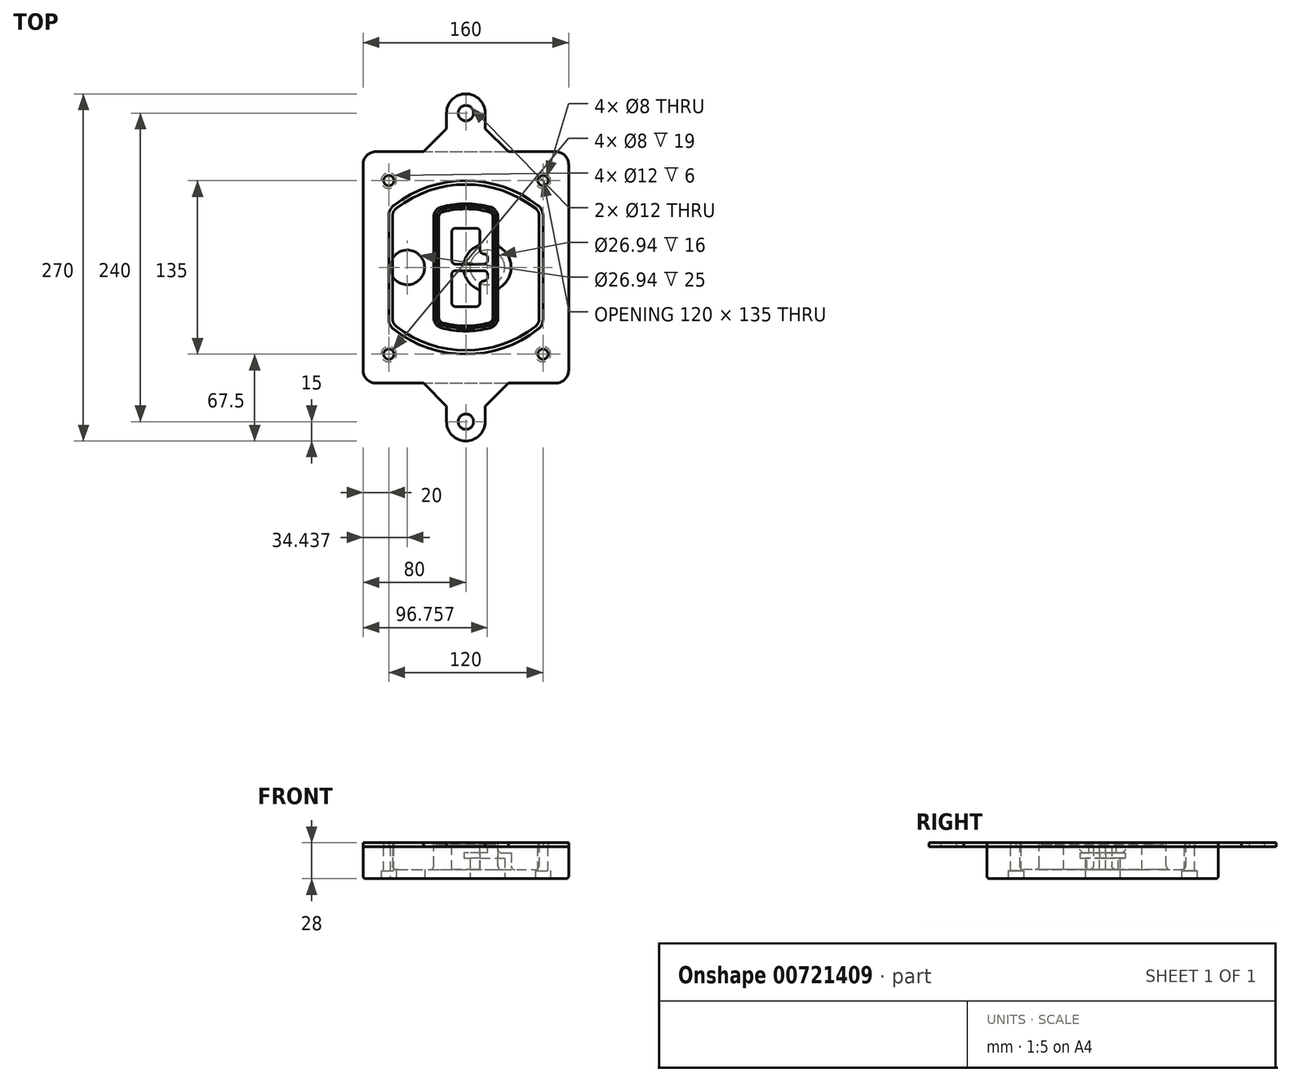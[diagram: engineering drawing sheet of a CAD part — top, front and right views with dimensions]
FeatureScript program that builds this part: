
annotation { "Feature Type Name" : "Feature", "Feature Type Description" : "" }
export const myFeature = defineFeature(function(context is Context, id is Id, definition is map)
    precondition{}
    {
        {
            var Q0;
            Q0=qCreatedBy(makeId("Top.planeOp"),FACE);
            var sketch = newSketch(context, id + "F0", { "sketchPlane" : qUnion([Q0])});
            skPoint(sketch, "E0.rect.middle", {"position": v(0, 0) * mm});
            skLineSegment(sketch, "E1.bottom", {"start": v(-70, -90) * mm, "end": v(70, -90) * mm});
            skLineSegment(sketch, "E1.top", {"start": v(-70, 90) * mm, "end": v(70, 90) * mm});
            skLineSegment(sketch, "E1.left", {"start": v(-80, -80) * mm, "end": v(-80, 80) * mm});
            skLineSegment(sketch, "E1.right", {"start": v(80, -80) * mm, "end": v(80, 80) * mm});
            skLineSegment(sketch, "E2", {"start": v(-80, 90) * mm, "end": v(80, -90) * mm, "construction": true});
            skLineSegment(sketch, "E3", {"start": v(80, 90) * mm, "end": v(-80, -90) * mm, "construction": true});
            skCircle(sketch, "E4", {"center": v(-60, 67.5) * mm, "radius": 4 * mm});
            skCircle(sketch, "E5", {"center": v(60, 67.5) * mm, "radius": 4 * mm});
            skCircle(sketch, "E6", {"center": v(60, -67.5) * mm, "radius": 4 * mm});
            skCircle(sketch, "E7", {"center": v(-60, -67.5) * mm, "radius": 4 * mm});
            skLineSegment(sketch, "E8", {"start": v(-60, 67.5) * mm, "end": v(60, 67.5) * mm, "construction": true});
            skLineSegment(sketch, "E9", {"start": v(60, 67.5) * mm, "end": v(60, -67.5) * mm, "construction": true});
            skLineSegment(sketch, "E10", {"start": v(60, -67.5) * mm, "end": v(-60, -67.5) * mm, "construction": true});
            skLineSegment(sketch, "E11", {"start": v(-60, -67.5) * mm, "end": v(-60, 67.5) * mm, "construction": true});
            skLineSegment(sketch, "E12", {"start": v(-60, 40.3) * mm, "end": v(-60, -40.3) * mm});
            skLineSegment(sketch, "E13", {"start": v(60, 40.3) * mm, "end": v(60, -40.3) * mm});
            skArc(sketch, "E14", {"start": v(56.15, 48.18) * mm, "mid": v(0, 67.5) * mm, "end": v(-56.15, 48.18) * mm});
            skArc(sketch, "E15", {"start": v(-56.15, -48.18) * mm, "mid": v(0, -67.5) * mm, "end": v(56.15, -48.18) * mm});
            skLineSegment(sketch, "E16", {"start": v(-60, 0) * mm, "end": v(60, 0) * mm, "construction": true});
            skPoint(sketch, "E17.visualSharp", {"position": v(-60, -45) * mm});
            skArc(sketch, "E17.filletArc", {"start": v(-60, -40.3) * mm, "mid": v(-58.99, -44.68) * mm, "end": v(-56.15, -48.18) * mm});
            skPoint(sketch, "E18.visualSharp", {"position": v(-60, 45) * mm});
            skArc(sketch, "E18.filletArc", {"start": v(-56.15, 48.18) * mm, "mid": v(-58.99, 44.68) * mm, "end": v(-60, 40.3) * mm});
            skPoint(sketch, "E19.visualSharp", {"position": v(60, 45) * mm});
            skArc(sketch, "E19.filletArc", {"start": v(60, 40.3) * mm, "mid": v(58.99, 44.68) * mm, "end": v(56.15, 48.18) * mm});
            skPoint(sketch, "E20.visualSharp", {"position": v(60, -45) * mm});
            skArc(sketch, "E20.filletArc", {"start": v(56.15, -48.18) * mm, "mid": v(58.99, -44.68) * mm, "end": v(60, -40.3) * mm});
            skPoint(sketch, "E21.visualSharp", {"position": v(-80, 90) * mm});
            skArc(sketch, "E21.filletArc", {"start": v(-70, 90) * mm, "mid": v(-77.07, 87.07) * mm, "end": v(-80, 80) * mm});
            skPoint(sketch, "E22.visualSharp", {"position": v(80, 90) * mm});
            skArc(sketch, "E22.filletArc", {"start": v(80, 80) * mm, "mid": v(77.07, 87.07) * mm, "end": v(70, 90) * mm});
            skPoint(sketch, "E23.visualSharp", {"position": v(80, -90) * mm});
            skArc(sketch, "E23.filletArc", {"start": v(70, -90) * mm, "mid": v(77.07, -87.07) * mm, "end": v(80, -80) * mm});
            skPoint(sketch, "E24.visualSharp", {"position": v(-80, -90) * mm});
            skArc(sketch, "E24.filletArc", {"start": v(-80, -80) * mm, "mid": v(-77.07, -87.07) * mm, "end": v(-70, -90) * mm});
            skArc(sketch, "E25.0", {"start": v(57, 40.3) * mm, "mid": v(56.3, 43.36) * mm, "end": v(54.3, 45.81) * mm});
            skLineSegment(sketch, "E25.1", {"start": v(57, 40.3) * mm, "end": v(57, -40.3) * mm});
            skArc(sketch, "E25.2", {"start": v(54.3, -45.81) * mm, "mid": v(56.3, -43.36) * mm, "end": v(57, -40.3) * mm});
            skArc(sketch, "E25.3", {"start": v(-54.3, -45.81) * mm, "mid": v(0, -64.5) * mm, "end": v(54.3, -45.81) * mm});
            skArc(sketch, "E25.4", {"start": v(-57, -40.3) * mm, "mid": v(-56.3, -43.36) * mm, "end": v(-54.3, -45.81) * mm});
            skArc(sketch, "E25.5", {"start": v(54.3, 45.81) * mm, "mid": v(0, 64.5) * mm, "end": v(-54.3, 45.81) * mm});
            skLineSegment(sketch, "E25.6", {"start": v(-57, 40.3) * mm, "end": v(-57, -40.3) * mm});
            skArc(sketch, "E25.7", {"start": v(-54.3, 45.81) * mm, "mid": v(-56.3, 43.36) * mm, "end": v(-57, 40.3) * mm});
            skArc(sketch, "E26.0", {"start": v(-58.62, 51.33) * mm, "mid": v(-62.58, 46.43) * mm, "end": v(-64, 40.3) * mm});
            skArc(sketch, "E26.1", {"start": v(58.62, 51.33) * mm, "mid": v(0, 71.5) * mm, "end": v(-58.62, 51.33) * mm});
            skArc(sketch, "E26.2", {"start": v(64, 40.3) * mm, "mid": v(62.58, 46.43) * mm, "end": v(58.62, 51.33) * mm});
            skLineSegment(sketch, "E26.3", {"start": v(64, 40.3) * mm, "end": v(64, -40.3) * mm});
            skArc(sketch, "E26.4", {"start": v(58.62, -51.33) * mm, "mid": v(62.58, -46.43) * mm, "end": v(64, -40.3) * mm});
            skLineSegment(sketch, "E26.5", {"start": v(-64, 40.3) * mm, "end": v(-64, -40.3) * mm});
            skArc(sketch, "E26.6", {"start": v(-58.62, -51.33) * mm, "mid": v(0, -71.5) * mm, "end": v(58.62, -51.33) * mm});
            skArc(sketch, "E26.7", {"start": v(-64, -40.3) * mm, "mid": v(-62.58, -46.43) * mm, "end": v(-58.62, -51.33) * mm});
            skSolve(sketch);
        }
        {
            var Q0;
            Q0=makeQuery(id+"F0.imprint","IMPRINT",FACE,{"disambiguationData":[TD([[makeQuery(id+"F0.imprint","IMPRINT",EDGE,{"derivedFrom":sQuery(id+"F0.wireOp",EDGE,"E1.bottom")}),1.0]])]});
            var Q1;
            Q1=makeQuery(id+"F0.imprint","IMPRINT",FACE,{"disambiguationData":[TD([[makeQuery(id+"F0.imprint","IMPRINT",EDGE,{"derivedFrom":sQuery(id+"F0.wireOp",EDGE,"E12")}),1.0]])]});
            var Q2;
            Q2=makeQuery(id+"F0.imprint","IMPRINT",FACE,{"disambiguationData":[TD([[makeQuery(id+"F0.imprint","IMPRINT",EDGE,{"derivedFrom":sQuery(id+"F0.wireOp",EDGE,"E25.0")}),1.0]])]});
            var Q3;
            Q3=makeQuery(id+"F0.imprint","IMPRINT",FACE,{"disambiguationData":[TD([[makeQuery(id+"F0.imprint","IMPRINT",EDGE,{"derivedFrom":sQuery(id+"F0.wireOp",EDGE,"E12")}),-1.0]])]});
            extrude(context, id + "F1", {"entities" : qUnion([Q0, Q1, Q2, Q3]), "oppositeDirection" : true, "depth" : 25 * mm});
        }
        {
            var Q0;
            Q0=makeQuery(id+"F0.imprint","IMPRINT",FACE,{"disambiguationData":[TD([[makeQuery(id+"F0.imprint","IMPRINT",EDGE,{"derivedFrom":sQuery(id+"F0.wireOp",EDGE,"E12")}),1.0]])]});
            extrude(context, id + "F2", {"entities" : qUnion([Q0]), "operationType" : NewBodyOperationType.ADD, "depth" : 3 * mm, "offsetDistance" : 25 * mm});
        }
        {
            var Q0;
            Q0=makeQuery(id+"F0.imprint","IMPRINT",FACE,{"disambiguationData":[TD([[makeQuery(id+"F0.imprint","IMPRINT",EDGE,{"derivedFrom":sQuery(id+"F0.wireOp",EDGE,"E25.0")}),1.0]])]});
            extrude(context, id + "F3", {"entities" : qUnion([Q0]), "operationType" : NewBodyOperationType.REMOVE, "oppositeDirection" : true, "depth" : 18 * mm});
        }
        {
            var Q0;
            Q0=makeQuery(id+"F2.opExtrude","CAP_FACE",FACE,{"disambiguationData":[OSD([sQuery(id+"F0.wireOp",EDGE,"E12"),sQuery(id+"F0.wireOp",EDGE,"E13"),sQuery(id+"F0.wireOp",EDGE,"E14"),sQuery(id+"F0.wireOp",EDGE,"E15"),sQuery(id+"F0.wireOp",EDGE,"E17.filletArc"),sQuery(id+"F0.wireOp",EDGE,"E18.filletArc"),sQuery(id+"F0.wireOp",EDGE,"E19.filletArc"),sQuery(id+"F0.wireOp",EDGE,"E20.filletArc"),sQuery(id+"F0.wireOp",EDGE,"E25.0"),sQuery(id+"F0.wireOp",EDGE,"E25.1"),sQuery(id+"F0.wireOp",EDGE,"E25.2"),sQuery(id+"F0.wireOp",EDGE,"E25.3"),sQuery(id+"F0.wireOp",EDGE,"E25.4"),sQuery(id+"F0.wireOp",EDGE,"E25.5"),sQuery(id+"F0.wireOp",EDGE,"E25.6"),sQuery(id+"F0.wireOp",EDGE,"E25.7")])],"isStart":false});
            var sketch = newSketch(context, id + "F4", { "sketchPlane" : qUnion([Q0])});
            skArc(sketch, "E27.0", {"start": v(-19.08, -46.97) * mm, "mid": v(0, -49.5) * mm, "end": v(19.08, -46.97) * mm});
            skArc(sketch, "E28.0", {"start": v(19.08, 46.97) * mm, "mid": v(0, 49.5) * mm, "end": v(-19.08, 46.97) * mm});
            skLineSegment(sketch, "E29", {"start": v(-25, 39.25) * mm, "end": v(-25, -39.25) * mm});
            skLineSegment(sketch, "E30", {"start": v(25, 39.25) * mm, "end": v(25, -39.25) * mm});
            skLineSegment(sketch, "E31", {"start": v(-25, 45.1) * mm, "end": v(25, 45.1) * mm, "construction": true});
            skLineSegment(sketch, "E32", {"start": v(-25, -45.1) * mm, "end": v(25, -45.1) * mm, "construction": true});
            skPoint(sketch, "E33.visualSharp", {"position": v(-25, 45.1) * mm});
            skArc(sketch, "E33.filletArc", {"start": v(-19.08, 46.97) * mm, "mid": v(-23.35, 44.11) * mm, "end": v(-25, 39.25) * mm});
            skPoint(sketch, "E34.visualSharp", {"position": v(25, 45.1) * mm});
            skArc(sketch, "E34.filletArc", {"start": v(25, 39.25) * mm, "mid": v(23.35, 44.11) * mm, "end": v(19.08, 46.97) * mm});
            skPoint(sketch, "E35.visualSharp", {"position": v(25, -45.1) * mm});
            skArc(sketch, "E35.filletArc", {"start": v(19.08, -46.97) * mm, "mid": v(23.35, -44.11) * mm, "end": v(25, -39.25) * mm});
            skPoint(sketch, "E36.visualSharp", {"position": v(-25, -45.1) * mm});
            skArc(sketch, "E36.filletArc", {"start": v(-25, -39.25) * mm, "mid": v(-23.35, -44.11) * mm, "end": v(-19.08, -46.97) * mm});
            skArc(sketch, "E37.0", {"start": v(54.3, 45.81) * mm, "mid": v(0, 64.5) * mm, "end": v(-54.3, 45.81) * mm});
            skArc(sketch, "E37.1", {"start": v(-54.3, 45.81) * mm, "mid": v(-56.3, 43.36) * mm, "end": v(-57, 40.3) * mm});
            skLineSegment(sketch, "E37.2", {"start": v(-57, 40.3) * mm, "end": v(-57, -40.3) * mm});
            skArc(sketch, "E37.3", {"start": v(-57, -40.3) * mm, "mid": v(-56.3, -43.36) * mm, "end": v(-54.3, -45.81) * mm});
            skArc(sketch, "E37.4", {"start": v(-54.3, -45.81) * mm, "mid": v(0, -64.5) * mm, "end": v(54.3, -45.81) * mm});
            skArc(sketch, "E37.5", {"start": v(54.3, -45.81) * mm, "mid": v(56.3, -43.36) * mm, "end": v(57, -40.3) * mm});
            skLineSegment(sketch, "E37.6", {"start": v(57, 40.3) * mm, "end": v(57, -40.3) * mm});
            skArc(sketch, "E37.7", {"start": v(57, 40.3) * mm, "mid": v(56.3, 43.36) * mm, "end": v(54.3, 45.81) * mm});
            skLineSegment(sketch, "E38.0", {"start": v(23, 39.25) * mm, "end": v(23, -39.25) * mm});
            skArc(sketch, "E38.1", {"start": v(18.56, -45.04) * mm, "mid": v(21.76, -42.9) * mm, "end": v(23, -39.25) * mm});
            skArc(sketch, "E38.2", {"start": v(-18.56, -45.04) * mm, "mid": v(0, -47.5) * mm, "end": v(18.56, -45.04) * mm});
            skArc(sketch, "E38.3", {"start": v(-23, -39.25) * mm, "mid": v(-21.76, -42.9) * mm, "end": v(-18.56, -45.04) * mm});
            skLineSegment(sketch, "E38.4", {"start": v(-23, 39.25) * mm, "end": v(-23, -39.25) * mm});
            skArc(sketch, "E38.5", {"start": v(23, 39.25) * mm, "mid": v(21.76, 42.9) * mm, "end": v(18.56, 45.04) * mm});
            skArc(sketch, "E38.6", {"start": v(-18.56, 45.04) * mm, "mid": v(-21.76, 42.9) * mm, "end": v(-23, 39.25) * mm});
            skArc(sketch, "E38.7", {"start": v(18.56, 45.04) * mm, "mid": v(0, 47.5) * mm, "end": v(-18.56, 45.04) * mm});
            skArc(sketch, "E39.0", {"start": v(21, 39.25) * mm, "mid": v(20.18, 41.68) * mm, "end": v(18.04, 43.1) * mm});
            skLineSegment(sketch, "E39.1", {"start": v(21, 39.25) * mm, "end": v(21, -39.25) * mm});
            skArc(sketch, "E39.2", {"start": v(18.04, -43.1) * mm, "mid": v(20.18, -41.68) * mm, "end": v(21, -39.25) * mm});
            skArc(sketch, "E39.3", {"start": v(-18.04, -43.1) * mm, "mid": v(0, -45.5) * mm, "end": v(18.04, -43.1) * mm});
            skArc(sketch, "E39.4", {"start": v(-21, -39.25) * mm, "mid": v(-20.18, -41.68) * mm, "end": v(-18.04, -43.1) * mm});
            skArc(sketch, "E39.5", {"start": v(18.04, 43.1) * mm, "mid": v(0, 45.5) * mm, "end": v(-18.04, 43.1) * mm});
            skLineSegment(sketch, "E39.6", {"start": v(-21, 39.25) * mm, "end": v(-21, -39.25) * mm});
            skArc(sketch, "E39.7", {"start": v(-18.04, 43.1) * mm, "mid": v(-20.18, 41.68) * mm, "end": v(-21, 39.25) * mm});
            skLineSegment(sketch, "E40", {"start": v(-25, 0) * mm, "end": v(25, 0) * mm, "construction": true});
            skLineSegment(sketch, "E41", {"start": v(-11, 5.5) * mm, "end": v(-11, 27.5) * mm});
            skLineSegment(sketch, "E42", {"start": v(-8, 30.5) * mm, "end": v(8, 30.5) * mm});
            skLineSegment(sketch, "E43", {"start": v(11, 27.5) * mm, "end": v(11, 13.5) * mm});
            skLineSegment(sketch, "E44", {"start": v(14, 10.5) * mm, "end": v(14, 10.5) * mm});
            skLineSegment(sketch, "E45", {"start": v(17, 7.5) * mm, "end": v(17, 5.5) * mm});
            skLineSegment(sketch, "E46", {"start": v(14, 2.5) * mm, "end": v(-8, 2.5) * mm});
            skPoint(sketch, "E47.visualSharp", {"position": v(-11, 30.5) * mm});
            skArc(sketch, "E47.filletArc", {"start": v(-8, 30.5) * mm, "mid": v(-10.12, 29.62) * mm, "end": v(-11, 27.5) * mm});
            skPoint(sketch, "E48.visualSharp", {"position": v(11, 30.5) * mm});
            skArc(sketch, "E48.filletArc", {"start": v(11, 27.5) * mm, "mid": v(10.12, 29.62) * mm, "end": v(8, 30.5) * mm});
            skPoint(sketch, "E49.visualSharp", {"position": v(11, 10.5) * mm});
            skArc(sketch, "E49.filletArc", {"start": v(11, 13.5) * mm, "mid": v(11.88, 11.38) * mm, "end": v(14, 10.5) * mm});
            skPoint(sketch, "E50.visualSharp", {"position": v(17, 10.5) * mm});
            skArc(sketch, "E50.filletArc", {"start": v(17, 7.5) * mm, "mid": v(16.12, 9.62) * mm, "end": v(14, 10.5) * mm});
            skPoint(sketch, "E51.visualSharp", {"position": v(17, 2.5) * mm});
            skArc(sketch, "E51.filletArc", {"start": v(14, 2.5) * mm, "mid": v(16.12, 3.38) * mm, "end": v(17, 5.5) * mm});
            skPoint(sketch, "E52.visualSharp", {"position": v(-11, 2.5) * mm});
            skArc(sketch, "E52.filletArc", {"start": v(-11, 5.5) * mm, "mid": v(-10.12, 3.38) * mm, "end": v(-8, 2.5) * mm});
            skLineSegment(sketch, "E53.0.MirrorCS", {"start": v(14, -2.5) * mm, "end": v(-8, -2.5) * mm});
            skArc(sketch, "E54.0.MirrorCS", {"start": v(-11, -5.5) * mm, "mid": v(-10.12, -3.38) * mm, "end": v(-8, -2.5) * mm});
            skLineSegment(sketch, "E55.0.MirrorCS", {"start": v(-11, -5.5) * mm, "end": v(-11, -27.5) * mm});
            skArc(sketch, "E56.0.MirrorCS", {"start": v(-8, -30.5) * mm, "mid": v(-10.12, -29.62) * mm, "end": v(-11, -27.5) * mm});
            skLineSegment(sketch, "E57.0.MirrorCS", {"start": v(-8, -30.5) * mm, "end": v(8, -30.5) * mm});
            skArc(sketch, "E58.0.MirrorCS", {"start": v(11, -27.5) * mm, "mid": v(10.12, -29.62) * mm, "end": v(8, -30.5) * mm});
            skLineSegment(sketch, "E59.0.MirrorCS", {"start": v(11, -27.5) * mm, "end": v(11, -13.5) * mm});
            skArc(sketch, "E60.0.MirrorCS", {"start": v(11, -13.5) * mm, "mid": v(11.88, -11.38) * mm, "end": v(14, -10.5) * mm});
            skArc(sketch, "E61.0.MirrorCS", {"start": v(17, -7.5) * mm, "mid": v(16.12, -9.62) * mm, "end": v(14, -10.5) * mm});
            skLineSegment(sketch, "E62.0.MirrorCS", {"start": v(17, -7.5) * mm, "end": v(17, -5.5) * mm});
            skArc(sketch, "E63.0.MirrorCS", {"start": v(14, -2.5) * mm, "mid": v(16.12, -3.38) * mm, "end": v(17, -5.5) * mm});
            skSolve(sketch);
        }
        {
            var Q0;
            Q0=makeQuery(id+"F4.imprint","IMPRINT",FACE,{"disambiguationData":[TD([[makeQuery(id+"F4.imprint","IMPRINT",EDGE,{"derivedFrom":sQuery(id+"F4.wireOp",EDGE,"E27.0")}),1.0]])]});
            var Q1;
            Q1=makeQuery(id+"F4.imprint","IMPRINT",FACE,{"disambiguationData":[TD([[makeQuery(id+"F4.imprint","IMPRINT",EDGE,{"derivedFrom":sQuery(id+"F4.wireOp",EDGE,"E38.0")}),-1.0]])]});
            var Q2;
            Q2=makeQuery(id+"F4.imprint","IMPRINT",FACE,{"disambiguationData":[TD([[makeQuery(id+"F4.imprint","IMPRINT",EDGE,{"derivedFrom":sQuery(id+"F4.wireOp",EDGE,"E39.0")}),1.0]])]});
            extrude(context, id + "F5", {"entities" : qUnion([Q0, Q1, Q2]), "operationType" : NewBodyOperationType.ADD, "endBound" : BoundingType.UP_TO_NEXT, "oppositeDirection" : true, "depth" : 25 * mm});
        }
        {
            var Q0;
            Q0=makeQuery(id+"F4.imprint","IMPRINT",FACE,{"disambiguationData":[TD([[makeQuery(id+"F4.imprint","IMPRINT",EDGE,{"derivedFrom":sQuery(id+"F4.wireOp",EDGE,"E38.0")}),-1.0]])]});
            extrude(context, id + "F6", {"entities" : qUnion([Q0]), "operationType" : NewBodyOperationType.REMOVE, "oppositeDirection" : true, "depth" : 2 * mm});
        }
        {
            var Q0;
            Q0=makeQuery(id+"F1.opExtrude","CAP_FACE",FACE,{"disambiguationData":[OSD([sQuery(id+"F0.wireOp",EDGE,"E1.bottom"),sQuery(id+"F0.wireOp",EDGE,"E1.top"),sQuery(id+"F0.wireOp",EDGE,"E1.left"),sQuery(id+"F0.wireOp",EDGE,"E1.right"),sQuery(id+"F0.wireOp",EDGE,"E4"),sQuery(id+"F0.wireOp",EDGE,"E5"),sQuery(id+"F0.wireOp",EDGE,"E6"),sQuery(id+"F0.wireOp",EDGE,"E7"),sQuery(id+"F0.wireOp",EDGE,"E21.filletArc"),sQuery(id+"F0.wireOp",EDGE,"E22.filletArc"),sQuery(id+"F0.wireOp",EDGE,"E23.filletArc"),sQuery(id+"F0.wireOp",EDGE,"E24.filletArc")])],"isStart":false});
            var sketch = newSketch(context, id + "F7", { "sketchPlane" : qUnion([Q0])});
            skCircle(sketch, "E64", {"center": v(16.76, 0) * mm, "radius": 13.47 * mm});
            skCircle(sketch, "E65", {"center": v(-45.56, 0) * mm, "radius": 13.47 * mm});
            skLineSegment(sketch, "E66", {"start": v(80, 0) * mm, "end": v(-80, 0) * mm});
            skCircle(sketch, "E67", {"center": v(16.76, 0) * mm, "radius": 18.47 * mm});
            skCircle(sketch, "E68", {"center": v(60, -67.5) * mm, "radius": 6 * mm});
            skCircle(sketch, "E69", {"center": v(-60, -67.5) * mm, "radius": 6 * mm});
            skCircle(sketch, "E70", {"center": v(-60, 67.5) * mm, "radius": 6 * mm});
            skCircle(sketch, "E71", {"center": v(60, 67.5) * mm, "radius": 6 * mm});
            skSolve(sketch);
        }
        {
            var Q0;
            {var subQ1=sQuery(id+"F7.wireOp",EDGE,"E66");var subQ4=sQuery(id+"F7.wireOp",EDGE,"E64");var subQ6=makeQuery(id+"F7.imprint","INTERSECT",VERTEX,{"disambiguationData":[OD(0.0)],"derivedFrom":[subQ4,subQ1]});Q0=makeQuery(id+"F7.imprint","IMPRINT",FACE,{"disambiguationData":[TD([[makeQuery(id+"F7.imprint","IMPRINT",EDGE,{"disambiguationData":[TD([[subQ6,-1.0]])],"derivedFrom":subQ4}),-1.0]])]});}
            var Q1;
            {var subQ0=sQuery(id+"F7.wireOp",EDGE,"E66");var subQ1=sQuery(id+"F7.wireOp",EDGE,"E64");var subQ3=makeQuery(id+"F7.imprint","INTERSECT",VERTEX,{"disambiguationData":[OD(0.0)],"derivedFrom":[subQ1,subQ0]});Q1=makeQuery(id+"F7.imprint","IMPRINT",FACE,{"disambiguationData":[TD([[makeQuery(id+"F7.imprint","IMPRINT",EDGE,{"disambiguationData":[TD([[subQ3,-1.0]])],"derivedFrom":subQ1}),1.0]])]});}
            var Q2;
            {var subQ0=sQuery(id+"F7.wireOp",EDGE,"E66");var subQ1=sQuery(id+"F7.wireOp",EDGE,"E64");var subQ3=makeQuery(id+"F7.imprint","INTERSECT",VERTEX,{"disambiguationData":[OD(0.0)],"derivedFrom":[subQ1,subQ0]});Q2=makeQuery(id+"F7.imprint","IMPRINT",FACE,{"disambiguationData":[TD([[makeQuery(id+"F7.imprint","IMPRINT",EDGE,{"disambiguationData":[TD([[subQ3,1.0]])],"derivedFrom":subQ1}),1.0]])]});}
            var Q3;
            {var subQ1=sQuery(id+"F7.wireOp",EDGE,"E66");var subQ4=sQuery(id+"F7.wireOp",EDGE,"E64");var subQ6=makeQuery(id+"F7.imprint","INTERSECT",VERTEX,{"disambiguationData":[OD(0.0)],"derivedFrom":[subQ4,subQ1]});Q3=makeQuery(id+"F7.imprint","IMPRINT",FACE,{"disambiguationData":[TD([[makeQuery(id+"F7.imprint","IMPRINT",EDGE,{"disambiguationData":[TD([[subQ6,1.0]])],"derivedFrom":subQ4}),-1.0]])]});}
            extrude(context, id + "F8", {"entities" : qUnion([Q0, Q1, Q2, Q3]), "operationType" : NewBodyOperationType.ADD, "oppositeDirection" : true, "depth" : 20 * mm});
        }
        {
            var Q0;
            {var subQ0=sQuery(id+"F7.wireOp",EDGE,"E66");var subQ1=sQuery(id+"F7.wireOp",EDGE,"E64");var subQ3=makeQuery(id+"F7.imprint","INTERSECT",VERTEX,{"disambiguationData":[OD(0.0)],"derivedFrom":[subQ1,subQ0]});Q0=makeQuery(id+"F7.imprint","IMPRINT",FACE,{"disambiguationData":[TD([[makeQuery(id+"F7.imprint","IMPRINT",EDGE,{"disambiguationData":[TD([[subQ3,-1.0]])],"derivedFrom":subQ1}),1.0]])]});}
            var Q1;
            {var subQ0=sQuery(id+"F7.wireOp",EDGE,"E66");var subQ1=sQuery(id+"F7.wireOp",EDGE,"E64");var subQ3=makeQuery(id+"F7.imprint","INTERSECT",VERTEX,{"disambiguationData":[OD(0.0)],"derivedFrom":[subQ1,subQ0]});Q1=makeQuery(id+"F7.imprint","IMPRINT",FACE,{"disambiguationData":[TD([[makeQuery(id+"F7.imprint","IMPRINT",EDGE,{"disambiguationData":[TD([[subQ3,1.0]])],"derivedFrom":subQ1}),1.0]])]});}
            extrude(context, id + "F9", {"entities" : qUnion([Q0, Q1]), "operationType" : NewBodyOperationType.REMOVE, "oppositeDirection" : true, "depth" : 16 * mm});
        }
        {
            var Q0;
            {var subQ0=sQuery(id+"F7.wireOp",EDGE,"E66");var subQ1=sQuery(id+"F7.wireOp",EDGE,"E65");var subQ3=makeQuery(id+"F7.imprint","INTERSECT",VERTEX,{"disambiguationData":[OD(0.0)],"derivedFrom":[subQ1,subQ0]});Q0=makeQuery(id+"F7.imprint","IMPRINT",FACE,{"disambiguationData":[TD([[makeQuery(id+"F7.imprint","IMPRINT",EDGE,{"disambiguationData":[TD([[subQ3,-1.0]])],"derivedFrom":subQ1}),1.0]])]});}
            var Q1;
            {var subQ0=sQuery(id+"F7.wireOp",EDGE,"E66");var subQ1=sQuery(id+"F7.wireOp",EDGE,"E65");var subQ3=makeQuery(id+"F7.imprint","INTERSECT",VERTEX,{"disambiguationData":[OD(0.0)],"derivedFrom":[subQ1,subQ0]});Q1=makeQuery(id+"F7.imprint","IMPRINT",FACE,{"disambiguationData":[TD([[makeQuery(id+"F7.imprint","IMPRINT",EDGE,{"disambiguationData":[TD([[subQ3,1.0]])],"derivedFrom":subQ1}),1.0]])]});}
            extrude(context, id + "F10", {"entities" : qUnion([Q0, Q1]), "operationType" : NewBodyOperationType.REMOVE, "oppositeDirection" : true, "depth" : 25 * mm});
        }
        {
            var Q0;
            Q0=makeQuery(id+"F7.imprint","IMPRINT",FACE,{"disambiguationData":[TD([[makeQuery(id+"F7.imprint","IMPRINT",EDGE,{"derivedFrom":sQuery(id+"F7.wireOp",EDGE,"E68")}),1.0]])]});
            var Q1;
            Q1=makeQuery(id+"F7.imprint","IMPRINT",FACE,{"disambiguationData":[TD([[makeQuery(id+"F7.imprint","IMPRINT",EDGE,{"derivedFrom":makeQuery(id+"F1.opExtrude","CAP_EDGE",EDGE,{"disambiguationData":[OSD([sQuery(id+"F0.wireOp",EDGE,"E5")])],"isStart":false})}),-1.0]])]});
            var Q2;
            Q2=makeQuery(id+"F7.imprint","IMPRINT",FACE,{"disambiguationData":[TD([[makeQuery(id+"F7.imprint","IMPRINT",EDGE,{"derivedFrom":sQuery(id+"F7.wireOp",EDGE,"E69")}),1.0]])]});
            var Q3;
            Q3=makeQuery(id+"F7.imprint","IMPRINT",FACE,{"disambiguationData":[TD([[makeQuery(id+"F7.imprint","IMPRINT",EDGE,{"derivedFrom":makeQuery(id+"F1.opExtrude","CAP_EDGE",EDGE,{"disambiguationData":[OSD([sQuery(id+"F0.wireOp",EDGE,"E4")])],"isStart":false})}),-1.0]])]});
            var Q4;
            Q4=makeQuery(id+"F7.imprint","IMPRINT",FACE,{"disambiguationData":[TD([[makeQuery(id+"F7.imprint","IMPRINT",EDGE,{"derivedFrom":sQuery(id+"F7.wireOp",EDGE,"E70")}),1.0]])]});
            var Q5;
            Q5=makeQuery(id+"F7.imprint","IMPRINT",FACE,{"disambiguationData":[TD([[makeQuery(id+"F7.imprint","IMPRINT",EDGE,{"derivedFrom":makeQuery(id+"F1.opExtrude","CAP_EDGE",EDGE,{"disambiguationData":[OSD([sQuery(id+"F0.wireOp",EDGE,"E7")])],"isStart":false})}),-1.0]])]});
            var Q6;
            Q6=makeQuery(id+"F7.imprint","IMPRINT",FACE,{"disambiguationData":[TD([[makeQuery(id+"F7.imprint","IMPRINT",EDGE,{"derivedFrom":sQuery(id+"F7.wireOp",EDGE,"E71")}),1.0]])]});
            var Q7;
            Q7=makeQuery(id+"F7.imprint","IMPRINT",FACE,{"disambiguationData":[TD([[makeQuery(id+"F7.imprint","IMPRINT",EDGE,{"derivedFrom":makeQuery(id+"F1.opExtrude","CAP_EDGE",EDGE,{"disambiguationData":[OSD([sQuery(id+"F0.wireOp",EDGE,"E6")])],"isStart":false})}),-1.0]])]});
            extrude(context, id + "F11", {"entities" : qUnion([Q0, Q1, Q2, Q3, Q4, Q5, Q6, Q7]), "operationType" : NewBodyOperationType.REMOVE, "oppositeDirection" : true, "depth" : 6 * mm});
        }
        {
            var Q0;
            Q0=makeQuery(id+"F9.boolean.opBoolean","COPY",FACE,{"derivedFrom":makeQuery(id+"F9.opExtrude","CAP_FACE",FACE,{"disambiguationData":[OSD([sQuery(id+"F7.wireOp",EDGE,"E64")])],"isStart":false})});
            var sketch = newSketch(context, id + "F12", { "sketchPlane" : qUnion([Q0])});
            skArc(sketch, "E72.0", {"start": v(11, 17.55) * mm, "mid": v(2.57, 11.82) * mm, "end": v(-1.54, 2.5) * mm});
            skArc(sketch, "E72.1", {"start": v(-1.54, -2.5) * mm, "mid": v(2.57, -11.82) * mm, "end": v(11, -17.55) * mm});
            skLineSegment(sketch, "E73", {"start": v(-1.54, -2.5) * mm, "end": v(14, -2.5) * mm});
            skLineSegment(sketch, "E74.0", {"start": v(14, 2.5) * mm, "end": v(-1.54, 2.5) * mm});
            skArc(sketch, "E74.1", {"start": v(14, 2.5) * mm, "mid": v(16.12, 3.38) * mm, "end": v(17, 5.5) * mm});
            skLineSegment(sketch, "E74.2", {"start": v(17, 7.5) * mm, "end": v(17, 5.5) * mm});
            skArc(sketch, "E74.3", {"start": v(17, 7.5) * mm, "mid": v(16.12, 9.62) * mm, "end": v(14, 10.5) * mm});
            skArc(sketch, "E74.4", {"start": v(11, 13.5) * mm, "mid": v(11.88, 11.38) * mm, "end": v(14, 10.5) * mm});
            skLineSegment(sketch, "E74.5", {"start": v(11, 17.55) * mm, "end": v(11, 13.5) * mm});
            skLineSegment(sketch, "E74.7", {"start": v(14, -2.5) * mm, "end": v(-1.54, -2.5) * mm});
            skArc(sketch, "E74.8", {"start": v(14, -2.5) * mm, "mid": v(16.12, -3.38) * mm, "end": v(17, -5.5) * mm});
            skLineSegment(sketch, "E74.9", {"start": v(17, -7.5) * mm, "end": v(17, -5.5) * mm});
            skArc(sketch, "E74.10", {"start": v(17, -7.5) * mm, "mid": v(16.12, -9.62) * mm, "end": v(14, -10.5) * mm});
            skArc(sketch, "E74.11", {"start": v(11, -13.5) * mm, "mid": v(11.88, -11.38) * mm, "end": v(14, -10.5) * mm});
            skLineSegment(sketch, "E74.12", {"start": v(11, -17.55) * mm, "end": v(11, -13.5) * mm});
            skPoint(sketch, "E75.orphan", {"position": v(11, -27.5) * mm});
            skPoint(sketch, "E76.orphan", {"position": v(-8, -2.5) * mm});
            skPoint(sketch, "E77.orphan", {"position": v(-8, 2.5) * mm});
            skPoint(sketch, "E78.orphan", {"position": v(11, 27.5) * mm});
            skSolve(sketch);
        }
        {
            var Q0;
            {var subQ7=sQuery(id+"F12.wireOp",EDGE,"E72.0");var subQ14=sQuery(id+"F12.wireOp",EDGE,"E72.1");var subQ16=sQuery(id+"F12.wireOp",EDGE,"E74.1");var subQ18=sQuery(id+"F12.wireOp",EDGE,"E74.8");Q0=qUnion([makeQuery(id+"F12.imprint","IMPRINT",FACE,{"disambiguationData":[TD([[makeQuery(id+"F12.imprint","IMPRINT",EDGE,{"derivedFrom":subQ7}),1.0]])]}),makeQuery(id+"F12.imprint","IMPRINT",FACE,{"disambiguationData":[TD([[makeQuery(id+"F12.imprint","IMPRINT",EDGE,{"derivedFrom":subQ14}),1.0]])]}),makeQuery(id+"F12.imprint","IMPRINT",FACE,{"disambiguationData":[TD([[makeQuery(id+"F12.imprint","IMPRINT",EDGE,{"derivedFrom":subQ16}),1.0]])]}),makeQuery(id+"F12.imprint","IMPRINT",FACE,{"disambiguationData":[TD([[makeQuery(id+"F12.imprint","IMPRINT",EDGE,{"derivedFrom":subQ18}),-1.0]])]})]);}
            var Q1;
            Q1=makeQuery(id+"F5.boolean.opBoolean","SPLIT",FACE,{"disambiguationData":[TD([makeQuery(id+"F5.opExtrude","SWEPT_FACE",FACE,{"disambiguationData":[OSD([sQuery(id+"F4.wireOp",EDGE,"E41")])]})])],"derivedFrom":makeQuery(id+"F3.boolean.opBoolean","COPY",FACE,{"derivedFrom":makeQuery(id+"F3.opExtrude","CAP_FACE",FACE,{"disambiguationData":[OSD([sQuery(id+"F0.wireOp",EDGE,"E25.0"),sQuery(id+"F0.wireOp",EDGE,"E25.1"),sQuery(id+"F0.wireOp",EDGE,"E25.2"),sQuery(id+"F0.wireOp",EDGE,"E25.3"),sQuery(id+"F0.wireOp",EDGE,"E25.4"),sQuery(id+"F0.wireOp",EDGE,"E25.5"),sQuery(id+"F0.wireOp",EDGE,"E25.6"),sQuery(id+"F0.wireOp",EDGE,"E25.7")])],"isStart":false})})});
            extrude(context, id + "F13", {"entities" : qUnion([Q0]), "operationType" : NewBodyOperationType.REMOVE, "endBound" : BoundingType.UP_TO_SURFACE, "endBoundEntityFace" : qUnion([Q1]), "depth" : 25 * mm});
        }
        {
            var Q0;
            Q0=makeQuery(id+"F3.boolean.opBoolean","COPY",EDGE,{"derivedFrom":makeQuery(id+"F3.opExtrude","CAP_EDGE",EDGE,{"disambiguationData":[OSD([sQuery(id+"F0.wireOp",EDGE,"E25.6")])],"isStart":false})});
            var Q1;
            Q1=makeQuery(id+"F8.boolean.opBoolean","INTERSECT",EDGE,{"derivedFrom":[makeQuery(id+"F5.opExtrude","SWEPT_FACE",FACE,{"disambiguationData":[OSD([sQuery(id+"F4.wireOp",EDGE,"E30")])]}),makeQuery(id+"F8.opExtrude","CAP_FACE",FACE,{"disambiguationData":[OSD([sQuery(id+"F7.wireOp",EDGE,"E67")])],"isStart":false})]});
            var Q2;
            Q2=makeQuery(id+"F8.boolean.opBoolean","INTERSECT",EDGE,{"disambiguationData":[OD(1.0)],"derivedFrom":[makeQuery(id+"F5.opExtrude","SWEPT_FACE",FACE,{"disambiguationData":[OSD([sQuery(id+"F4.wireOp",EDGE,"E30")])]}),makeQuery(id+"F8.opExtrude","SWEPT_FACE",FACE,{"disambiguationData":[OSD([sQuery(id+"F7.wireOp",EDGE,"E67")])]})]});
            var Q3;
            {var subQ0=sQuery(id+"F4.wireOp",EDGE,"E30");Q3=makeQuery(id+"F8.boolean.opBoolean","SPLIT",EDGE,{"disambiguationData":[TD([makeQuery(id+"F5.opExtrude","SWEPT_FACE",FACE,{"disambiguationData":[OSD([sQuery(id+"F4.wireOp",EDGE,"E35.filletArc")])]})])],"derivedFrom":makeQuery(id+"F5.opExtrude","CAP_EDGE",EDGE,{"disambiguationData":[OSD([subQ0])],"isStart":false})});}
            var Q4;
            {var subQ0=sQuery(id+"F0.wireOp",EDGE,"E25.7");var subQ1=sQuery(id+"F0.wireOp",EDGE,"E25.1");var subQ2=sQuery(id+"F0.wireOp",EDGE,"E25.6");var subQ3=sQuery(id+"F0.wireOp",EDGE,"E25.5");var subQ4=sQuery(id+"F0.wireOp",EDGE,"E25.4");var subQ5=sQuery(id+"F0.wireOp",EDGE,"E25.0");var subQ6=sQuery(id+"F0.wireOp",EDGE,"E25.2");var subQ7=sQuery(id+"F0.wireOp",EDGE,"E25.3");Q4=makeQuery(id+"F8.boolean.opBoolean","INTERSECT",EDGE,{"derivedFrom":[makeQuery(id+"F5.boolean.opBoolean","SPLIT",FACE,{"disambiguationData":[TD([makeQuery(id+"F2.opExtrude","SWEPT_FACE",FACE,{"disambiguationData":[OSD([subQ5])]})])],"derivedFrom":makeQuery(id+"F3.boolean.opBoolean","COPY",FACE,{"derivedFrom":makeQuery(id+"F3.opExtrude","CAP_FACE",FACE,{"disambiguationData":[OSD([subQ5,subQ1,subQ6,subQ7,subQ4,subQ3,subQ2,subQ0])],"isStart":false})})}),makeQuery(id+"F8.opExtrude","SWEPT_FACE",FACE,{"disambiguationData":[OSD([sQuery(id+"F7.wireOp",EDGE,"E67")])]})]});}
            var Q5;
            Q5=makeQuery(id+"F8.boolean.opBoolean","INTERSECT",EDGE,{"disambiguationData":[OD(0.0)],"derivedFrom":[makeQuery(id+"F5.opExtrude","SWEPT_FACE",FACE,{"disambiguationData":[OSD([sQuery(id+"F4.wireOp",EDGE,"E30")])]}),makeQuery(id+"F8.opExtrude","SWEPT_FACE",FACE,{"disambiguationData":[OSD([sQuery(id+"F7.wireOp",EDGE,"E67")])]})]});
            fillet(context, id + "F14", {"entities" : qUnion([Q0, Q1, Q2, Q3, Q4, Q5]), "radius" : 3 * mm, "tangentPropagation" : true, "allowEdgeOverflow" : false});
        }
        {
            var Q0;
            Q0=makeQuery(id+"F1.opExtrude","CAP_EDGE",EDGE,{"disambiguationData":[OSD([sQuery(id+"F0.wireOp",EDGE,"E1.bottom")])],"isStart":false});
            fillet(context, id + "F15", {"entities" : qUnion([Q0]), "radius" : 2 * mm, "tangentPropagation" : true, "allowEdgeOverflow" : false});
        }
        {
            var Q0;
            {var subQ0=sQuery(id+"F0.wireOp",EDGE,"E21.filletArc");var subQ1=sQuery(id+"F0.wireOp",EDGE,"E7");var subQ2=sQuery(id+"F0.wireOp",EDGE,"E6");var subQ3=sQuery(id+"F0.wireOp",EDGE,"E5");var subQ4=sQuery(id+"F0.wireOp",EDGE,"E4");var subQ5=sQuery(id+"F0.wireOp",EDGE,"E22.filletArc");var subQ6=sQuery(id+"F0.wireOp",EDGE,"E1.bottom");var subQ7=sQuery(id+"F0.wireOp",EDGE,"E1.right");var subQ8=sQuery(id+"F0.wireOp",EDGE,"E1.top");var subQ9=sQuery(id+"F0.wireOp",EDGE,"E1.left");var subQ10=sQuery(id+"F0.wireOp",EDGE,"E23.filletArc");var subQ11=sQuery(id+"F0.wireOp",EDGE,"E24.filletArc");Q0=makeQuery(id+"F2.boolean.opBoolean","SPLIT",FACE,{"disambiguationData":[TD([makeQuery(id+"F1.opExtrude","SWEPT_FACE",FACE,{"disambiguationData":[OSD([subQ6])]})])],"derivedFrom":makeQuery(id+"F1.opExtrude","CAP_FACE",FACE,{"disambiguationData":[OSD([subQ6,subQ8,subQ9,subQ7,subQ4,subQ3,subQ2,subQ1,subQ0,subQ5,subQ10,subQ11])],"isStart":true})});}
            var sketch = newSketch(context, id + "F16", { "sketchPlane" : qUnion([Q0])});
            skArc(sketch, "E79.0", {"start": v(56.15, 48.18) * mm, "mid": v(0, 67.5) * mm, "end": v(-56.15, 48.18) * mm});
            skLineSegment(sketch, "E79.2", {"start": v(80, -80) * mm, "end": v(80, 80) * mm});
            skArc(sketch, "E79.3", {"start": v(80, 80) * mm, "mid": v(77.07, 87.07) * mm, "end": v(70, 90) * mm});
            skLineSegment(sketch, "E79.4", {"start": v(-70, 90) * mm, "end": v(70, 90) * mm});
            skArc(sketch, "E79.5", {"start": v(-70, 90) * mm, "mid": v(-77.07, 87.07) * mm, "end": v(-80, 80) * mm});
            skLineSegment(sketch, "E79.6", {"start": v(-80, -80) * mm, "end": v(-80, 80) * mm});
            skArc(sketch, "E79.7", {"start": v(-80, -80) * mm, "mid": v(-77.07, -87.07) * mm, "end": v(-70, -90) * mm});
            skLineSegment(sketch, "E79.8", {"start": v(-70, -90) * mm, "end": v(70, -90) * mm});
            skArc(sketch, "E79.9", {"start": v(70, -90) * mm, "mid": v(77.07, -87.07) * mm, "end": v(80, -80) * mm});
            skCircle(sketch, "E79.10", {"center": v(60, -67.5) * mm, "radius": 4 * mm});
            skCircle(sketch, "E79.11", {"center": v(60, 67.5) * mm, "radius": 4 * mm});
            skCircle(sketch, "E79.12", {"center": v(-60, 67.5) * mm, "radius": 4 * mm});
            skCircle(sketch, "E79.13", {"center": v(-60, -67.5) * mm, "radius": 4 * mm});
            skLineSegment(sketch, "E79.14", {"start": v(-60, 40.3) * mm, "end": v(-60, -40.3) * mm});
            skArc(sketch, "E79.15", {"start": v(-56.15, -48.18) * mm, "mid": v(0, -67.5) * mm, "end": v(56.15, -48.18) * mm});
            skLineSegment(sketch, "E79.16", {"start": v(60, 40.3) * mm, "end": v(60, -40.3) * mm});
            skArc(sketch, "E80", {"start": v(15, 120) * mm, "mid": v(0, 135) * mm, "end": v(-15, 120) * mm});
            skLineSegment(sketch, "E81", {"start": v(-15, 120) * mm, "end": v(-15, 108) * mm});
            skLineSegment(sketch, "E82", {"start": v(15, 120) * mm, "end": v(15, 108) * mm});
            skCircle(sketch, "E83", {"center": v(0, 120) * mm, "radius": 6 * mm});
            skLineSegment(sketch, "E84", {"start": v(0, 120) * mm, "end": v(0, 90) * mm, "construction": true});
            skLineSegment(sketch, "E85.MirrorCS", {"start": v(64.25, 74.25) * mm, "end": v(-64.25, 74.25) * mm});
            skLineSegment(sketch, "E86", {"start": v(-15, 108) * mm, "end": v(-33, 90) * mm});
            skLineSegment(sketch, "E87", {"start": v(15, 108) * mm, "end": v(33, 90) * mm});
            skLineSegment(sketch, "E88", {"start": v(-80, 0) * mm, "end": v(80, 0) * mm, "construction": true});
            skLineSegment(sketch, "E89.MirrorCS", {"start": v(64.25, -74.25) * mm, "end": v(-64.25, -74.25) * mm});
            skLineSegment(sketch, "E90.MirrorCS", {"start": v(15, -108) * mm, "end": v(33, -90) * mm});
            skArc(sketch, "E91.MirrorCS", {"start": v(15, -120) * mm, "mid": v(0, -135) * mm, "end": v(-15, -120) * mm});
            skLineSegment(sketch, "E92.MirrorCS", {"start": v(15, -120) * mm, "end": v(15, -108) * mm});
            skLineSegment(sketch, "E93.MirrorCS", {"start": v(-15, -120) * mm, "end": v(-15, -108) * mm});
            skCircle(sketch, "E94.MirrorC", {"center": v(0, -120) * mm, "radius": 6 * mm});
            skLineSegment(sketch, "E95.MirrorCS", {"start": v(0, -120) * mm, "end": v(0, -90) * mm, "construction": true});
            skLineSegment(sketch, "E96.MirrorCS", {"start": v(-15, -108) * mm, "end": v(-33, -90) * mm});
            skSolve(sketch);
        }
        {
            var Q0;
            Q0=makeQuery(id+"F16.imprint","IMPRINT",FACE,{"disambiguationData":[TD([[makeQuery(id+"F16.imprint","IMPRINT",EDGE,{"derivedFrom":sQuery(id+"F16.wireOp",EDGE,"E79.0")}),-1.0]])]});
            var Q1;
            Q1=makeQuery(id+"F16.imprint","IMPRINT",FACE,{"disambiguationData":[TD([[makeQuery(id+"F16.imprint","IMPRINT",EDGE,{"derivedFrom":sQuery(id+"F16.wireOp",EDGE,"E80")}),1.0]])]});
            var Q2;
            {var subQ0=sQuery(id+"F16.wireOp",EDGE,"E90.MirrorCS");Q2=makeQuery(id+"F16.imprint","IMPRINT",FACE,{"disambiguationData":[TD([[makeQuery(id+"F16.imprint","IMPRINT",EDGE,{"derivedFrom":subQ0}),1.0]])]});}
            var Q3;
            Q3=makeQuery(id+"F2.opExtrude","CAP_FACE",FACE,{"disambiguationData":[OSD([sQuery(id+"F0.wireOp",EDGE,"E12"),sQuery(id+"F0.wireOp",EDGE,"E13"),sQuery(id+"F0.wireOp",EDGE,"E14"),sQuery(id+"F0.wireOp",EDGE,"E15"),sQuery(id+"F0.wireOp",EDGE,"E17.filletArc"),sQuery(id+"F0.wireOp",EDGE,"E18.filletArc"),sQuery(id+"F0.wireOp",EDGE,"E19.filletArc"),sQuery(id+"F0.wireOp",EDGE,"E20.filletArc"),sQuery(id+"F0.wireOp",EDGE,"E25.0"),sQuery(id+"F0.wireOp",EDGE,"E25.1"),sQuery(id+"F0.wireOp",EDGE,"E25.2"),sQuery(id+"F0.wireOp",EDGE,"E25.3"),sQuery(id+"F0.wireOp",EDGE,"E25.4"),sQuery(id+"F0.wireOp",EDGE,"E25.5"),sQuery(id+"F0.wireOp",EDGE,"E25.6"),sQuery(id+"F0.wireOp",EDGE,"E25.7")])],"isStart":false});
            extrude(context, id + "F17", {"entities" : qUnion([Q0, Q1, Q2]), "endBound" : BoundingType.UP_TO_SURFACE, "depth" : 25 * mm, "endBoundEntityFace" : qUnion([Q3]), "offsetDistance" : 25 * mm});
        }
    });
